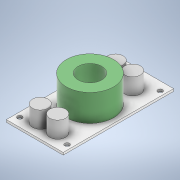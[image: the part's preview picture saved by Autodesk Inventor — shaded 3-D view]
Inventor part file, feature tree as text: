
AUTODESK INVENTOR PART (.ipt)
format: ipt  version: 2020 (Build 240168000, 168)  size: 205,824 bytes
history: native  units: mm
features: extrude x3, sketch x3, other x2
ambient origin geometry x8: Origin, YZ Plane, XZ Plane, XY Plane, X Axis, Y Axis, Z Axis, Center Point
bodies: Body1 (feature_tree)
feature tree (8):
  other  "Твердое тело1"
  extrude  "Выдавливание1"  Depth=36.0mm
  extrude  "Выдавливание2"  Depth=70.0mm
  extrude  "Выдавливание3"  Depth=30.0mm
  other  "РабПлоскость1"
  sketch  "Эскиз1"
  sketch  "Эскиз2"
  sketch  "Эскиз4"
